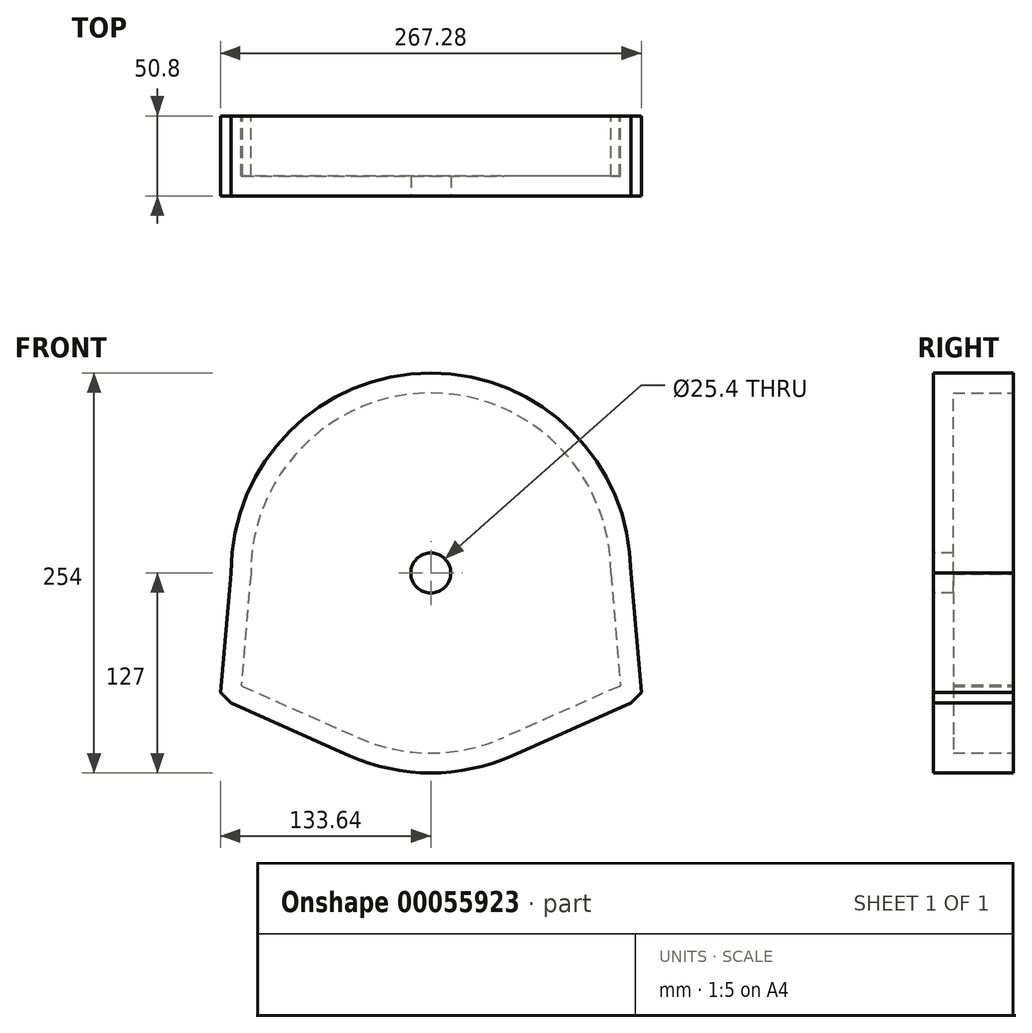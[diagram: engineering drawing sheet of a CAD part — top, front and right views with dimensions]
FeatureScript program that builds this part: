
annotation { "Feature Type Name" : "Feature", "Feature Type Description" : "" }
export const myFeature = defineFeature(function(context is Context, id is Id, definition is map)
    precondition{}
    {
        {
            var Q0;
            Q0=qCreatedBy(makeId("Front.planeOp"),FACE);
            var sketch = newSketch(context, id + "F0", { "sketchPlane" : qUnion([Q0])});
            skCircle(sketch, "E0", {"center": v(0, 0) * mm, "radius": 127 * mm});
            skLineSegment(sketch, "E1", {"start": v(-127, 0) * mm, "end": v(-133.64, -75.91) * mm});
            skLineSegment(sketch, "E2", {"start": v(-127, 0) * mm, "end": v(-127, -82.55) * mm});
            skLineSegment(sketch, "E3", {"start": v(-133.64, -75.91) * mm, "end": v(-127, -82.55) * mm});
            skLineSegment(sketch, "E4", {"start": v(-127, -82.55) * mm, "end": v(-51.56, -116.06) * mm});
            skLineSegment(sketch, "E5", {"start": v(0, 0) * mm, "end": v(0, -127) * mm});
            skLineSegment(sketch, "E6.MirrorCS", {"start": v(127, 0) * mm, "end": v(133.64, -75.91) * mm});
            skLineSegment(sketch, "E7.MirrorCS", {"start": v(133.64, -75.91) * mm, "end": v(127, -82.55) * mm});
            skLineSegment(sketch, "E8.MirrorCS", {"start": v(127, -82.55) * mm, "end": v(51.56, -116.06) * mm});
            skSolve(sketch);
        }
        {
            var Q0;
            Q0=makeQuery(id+"F0.imprint","IMPRINT",FACE,{"disambiguationData":[TD([[makeQuery(id+"F0.imprint","IMPRINT",EDGE,{"derivedFrom":sQuery(id+"F0.wireOp",EDGE,"E1")}),1.0]])]});
            var Q1;
            {var subQ0=sQuery(id+"F0.wireOp",EDGE,"E2");Q1=makeQuery(id+"F0.imprint","IMPRINT",FACE,{"disambiguationData":[TD([[makeQuery(id+"F0.imprint","IMPRINT",EDGE,{"derivedFrom":subQ0}),1.0]])]});}
            var Q2;
            {var subQ0=sQuery(id+"F0.wireOp",EDGE,"E0");var subQ1=makeQuery(id+"F0.imprint","IMPRINT",VERTEX,{"derivedFrom":subQ0});Q2=makeQuery(id+"F0.imprint","IMPRINT",FACE,{"disambiguationData":[TD([[makeQuery(id+"F0.imprint","IMPRINT",EDGE,{"disambiguationData":[TD([[subQ1,1.0]])],"derivedFrom":subQ0}),1.0]])]});}
            var Q3;
            {var subQ0=sQuery(id+"F0.wireOp",EDGE,"E6.MirrorCS");Q3=makeQuery(id+"F0.imprint","IMPRINT",FACE,{"disambiguationData":[TD([[makeQuery(id+"F0.imprint","IMPRINT",EDGE,{"derivedFrom":subQ0}),-1.0]])]});}
            extrude(context, id + "F1", {"entities" : qUnion([Q0, Q1, Q2, Q3]), "depth" : 50.8 * mm});
        }
        {
            var Q0;
            Q0=makeQuery(id+"F1.opExtrude","CAP_FACE",FACE,{"disambiguationData":[OSD([sQuery(id+"F0.wireOp",EDGE,"E0"),sQuery(id+"F0.wireOp",EDGE,"E1"),sQuery(id+"F0.wireOp",EDGE,"E3"),sQuery(id+"F0.wireOp",EDGE,"E4"),sQuery(id+"F0.wireOp",EDGE,"E6.MirrorCS"),sQuery(id+"F0.wireOp",EDGE,"E7.MirrorCS"),sQuery(id+"F0.wireOp",EDGE,"E8.MirrorCS")])],"isStart":true});
            shell(context, id + "F2", {"entities" : qUnion([Q0]), "thickness" : 12.7 * mm});
        }
        {
            var Q0;
            Q0=makeQuery(id+"F1.opExtrude","CAP_FACE",FACE,{"disambiguationData":[OSD([sQuery(id+"F0.wireOp",EDGE,"E0"),sQuery(id+"F0.wireOp",EDGE,"E1"),sQuery(id+"F0.wireOp",EDGE,"E3"),sQuery(id+"F0.wireOp",EDGE,"E4"),sQuery(id+"F0.wireOp",EDGE,"E6.MirrorCS"),sQuery(id+"F0.wireOp",EDGE,"E7.MirrorCS"),sQuery(id+"F0.wireOp",EDGE,"E8.MirrorCS")])],"isStart":false});
            var sketch = newSketch(context, id + "F3", { "sketchPlane" : qUnion([Q0])});
            skCircle(sketch, "E9", {"center": v(0, 0) * mm, "radius": 12.7 * mm});
            skSolve(sketch);
        }
        {
            var Q0;
            Q0 = qSketchRegion(id + "F3", true);
            extrude(context, id + "F4", {"entities" : qUnion([Q0]), "operationType" : NewBodyOperationType.REMOVE, "endBound" : BoundingType.THROUGH_ALL, "oppositeDirection" : true, "depth" : 25.4 * mm});
        }
    });
